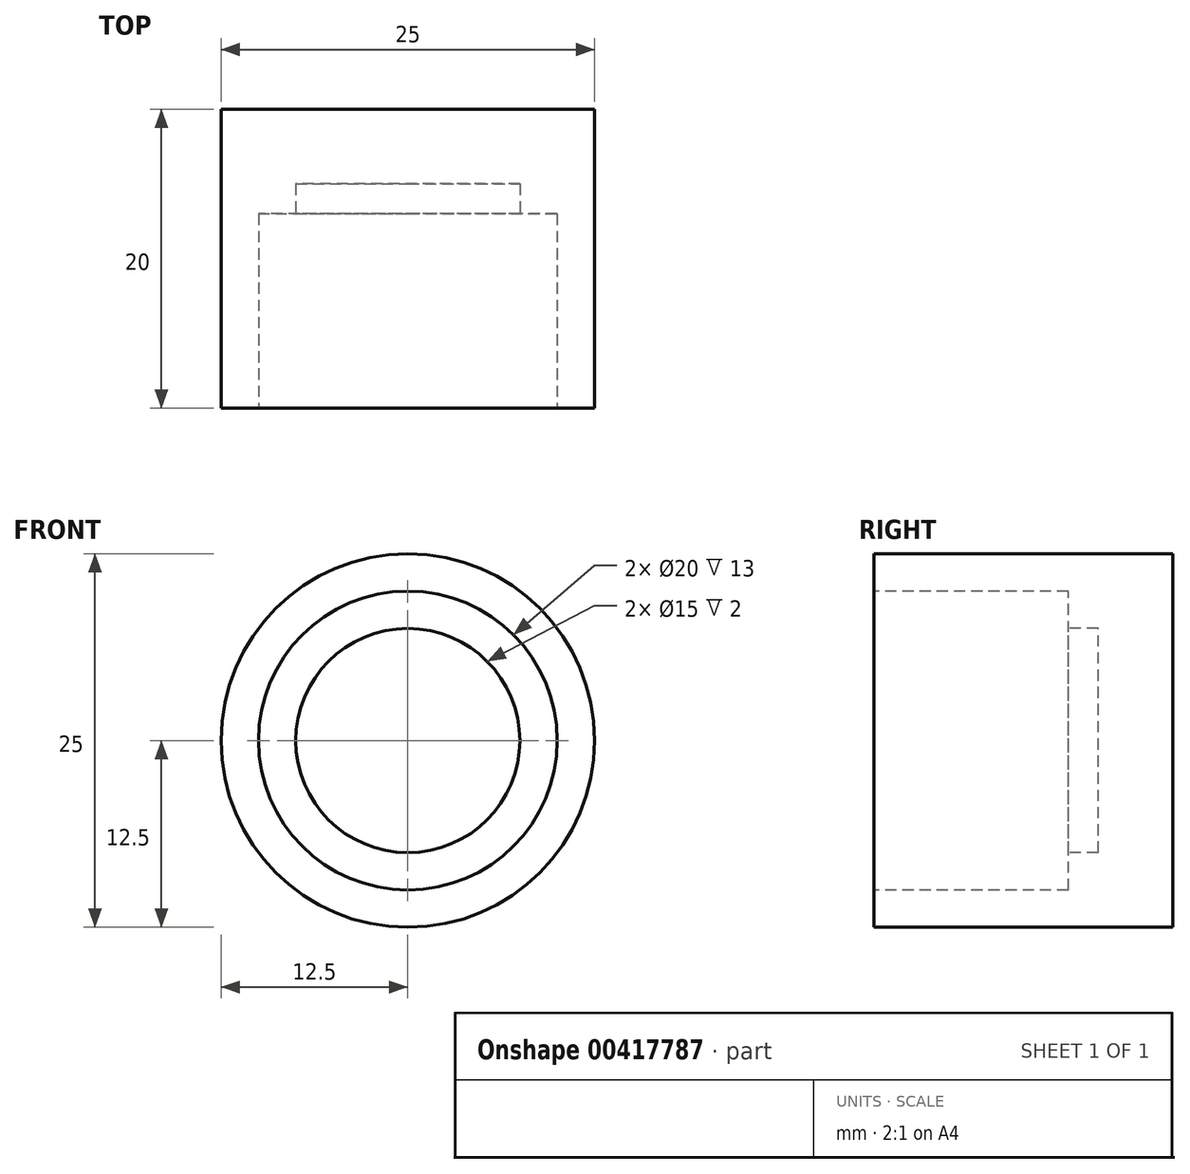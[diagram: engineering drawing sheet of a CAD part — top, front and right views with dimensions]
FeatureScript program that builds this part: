
annotation { "Feature Type Name" : "Feature", "Feature Type Description" : "" }
export const myFeature = defineFeature(function(context is Context, id is Id, definition is map)
    precondition{}
    {
        {
            var Q0;
            Q0=qCreatedBy(makeId("Front.planeOp"),FACE);
            var sketch = newSketch(context, id + "F0", { "sketchPlane" : qUnion([Q0])});
            skCircle(sketch, "E0", {"center": v(0, 0) * mm, "radius": 12.5 * mm});
            skSolve(sketch);
        }
        {
            var Q0;
            Q0=makeQuery(id+"F0.imprint","IMPRINT",FACE,{"disambiguationData":[TD([[makeQuery(id+"F0.imprint","IMPRINT",EDGE,{"derivedFrom":sQuery(id+"F0.wireOp",EDGE,"E0")}),1.0]])]});
            extrude(context, id + "F1", {"entities" : qUnion([Q0]), "depth" : 20 * mm});
        }
        {
            var Q0;
            Q0=makeQuery(id+"F1.opExtrude","CAP_FACE",FACE,{"disambiguationData":[OSD([sQuery(id+"F0.wireOp",EDGE,"E0")])],"isStart":false});
            var sketch = newSketch(context, id + "F2", { "sketchPlane" : qUnion([Q0])});
            skCircle(sketch, "E1", {"center": v(0, 0) * mm, "radius": 7.5 * mm});
            skSolve(sketch);
        }
        {
            var Q0;
            Q0=makeQuery(id+"F2.imprint","IMPRINT",FACE,{"disambiguationData":[TD([[makeQuery(id+"F2.imprint","IMPRINT",EDGE,{"derivedFrom":sQuery(id+"F2.wireOp",EDGE,"E1")}),1.0]])]});
            extrude(context, id + "F3", {"entities" : qUnion([Q0]), "operationType" : NewBodyOperationType.REMOVE, "oppositeDirection" : true, "depth" : 15 * mm});
        }
        {
            var Q0;
            Q0=makeQuery(id+"F1.opExtrude","CAP_FACE",FACE,{"disambiguationData":[OSD([sQuery(id+"F0.wireOp",EDGE,"E0")])],"isStart":false});
            var sketch = newSketch(context, id + "F4", { "sketchPlane" : qUnion([Q0])});
            skCircle(sketch, "E2", {"center": v(0, 0) * mm, "radius": 10 * mm});
            skSolve(sketch);
        }
        {
            var Q0;
            Q0=makeQuery(id+"F4.imprint","IMPRINT",FACE,{"disambiguationData":[TD([[makeQuery(id+"F4.imprint","IMPRINT",EDGE,{"derivedFrom":sQuery(id+"F4.wireOp",EDGE,"E2")}),1.0]])]});
            extrude(context, id + "F5", {"entities" : qUnion([Q0]), "operationType" : NewBodyOperationType.REMOVE, "oppositeDirection" : true, "depth" : 13 * mm});
        }
    });
